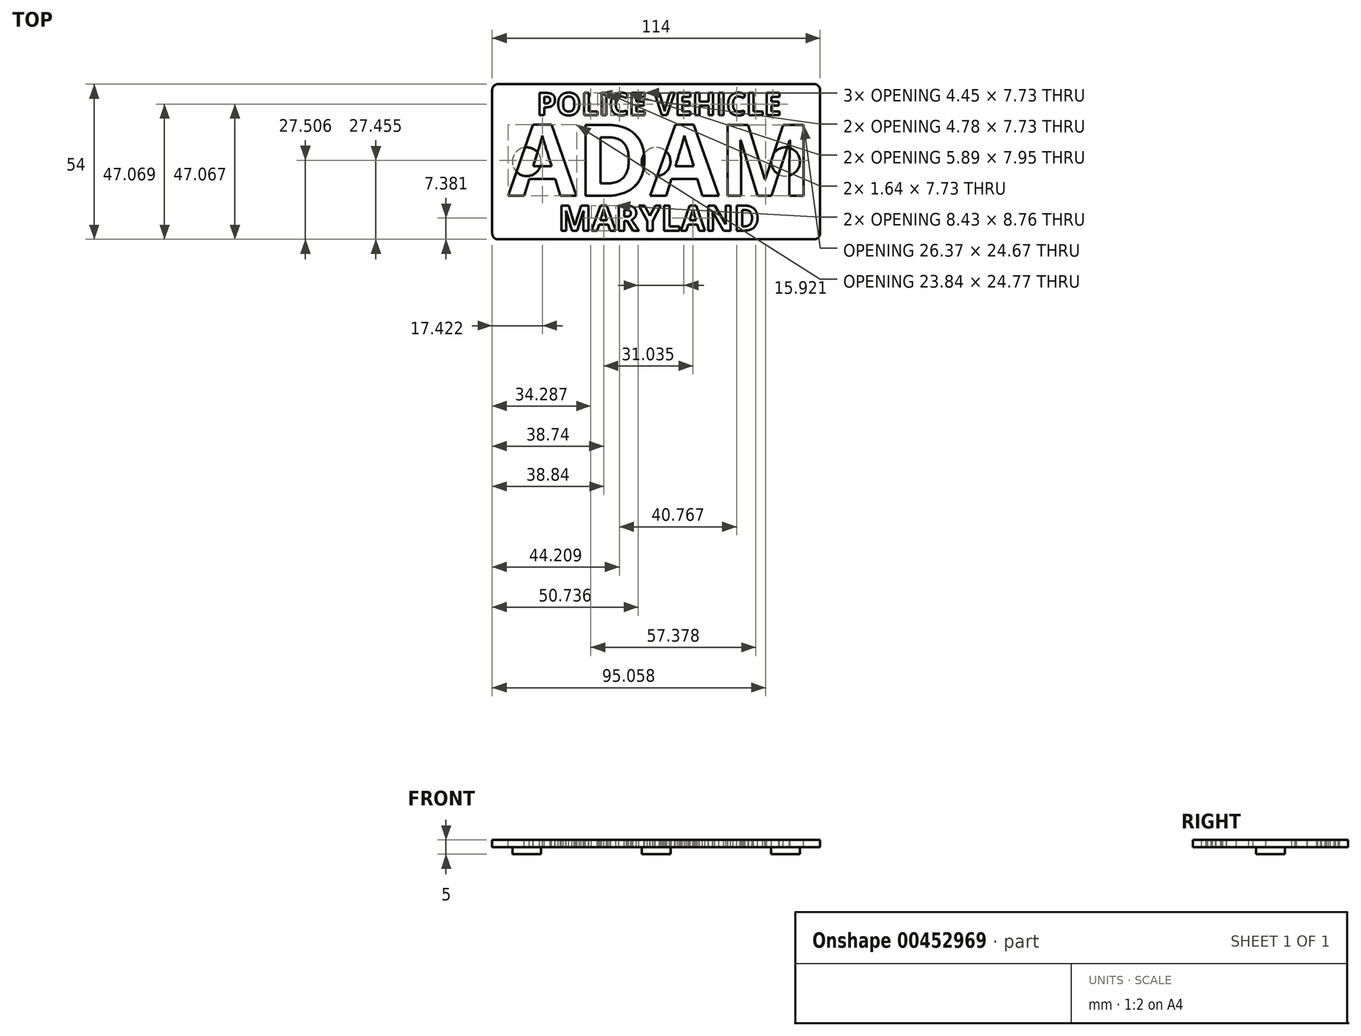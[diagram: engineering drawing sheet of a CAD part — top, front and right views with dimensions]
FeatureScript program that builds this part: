
annotation { "Feature Type Name" : "Feature", "Feature Type Description" : "" }
export const myFeature = defineFeature(function(context is Context, id is Id, definition is map)
    precondition{}
    {
        {
            var Q0;
            Q0=qCreatedBy(makeId("Top.planeOp"),FACE);
            var sketch = newSketch(context, id + "F0", { "sketchPlane" : qUnion([Q0])});
            skCircle(sketch, "E0", {"center": v(0, 0) * mm, "radius": 5 * mm});
            skCircle(sketch, "E1", {"center": v(-45, 0) * mm, "radius": 5 * mm});
            skCircle(sketch, "E2.MirrorC", {"center": v(45, 0) * mm, "radius": 5 * mm});
            skSolve(sketch);
        }
        {
            var Q0;
            Q0 = qSketchRegion(id + "F0", true);
            extrude(context, id + "F1", {"entities" : qUnion([Q0]), "depth" : 2.5 * mm, "offsetDistance" : 25 * mm});
        }
        {
            var Q0;
            Q0=qCreatedBy(makeId("Top.planeOp"),FACE);
            cPlane(context, id + "F2", {"entities" : qUnion([Q0]), "cplaneType" : CPlaneType.OFFSET, "offset" : 2.5 * mm, "width" : 150 * mm, "height" : 150 * mm});
        }
        {
            var Q0;
            Q0=qCreatedBy(id+"F2.planeOp",FACE);
            var sketch = newSketch(context, id + "F3", { "sketchPlane" : qUnion([Q0])});
            skLineSegment(sketch, "E3.bottom", {"start": v(57, -27) * mm, "end": v(-57, -27) * mm});
            skLineSegment(sketch, "E3.top", {"start": v(57, 27) * mm, "end": v(-57, 27) * mm});
            skLineSegment(sketch, "E3.left", {"start": v(57, -27) * mm, "end": v(57, 27) * mm});
            skLineSegment(sketch, "E3.right", {"start": v(-57, -27) * mm, "end": v(-57, 27) * mm});
            skPoint(sketch, "E3.middle", {"position": v(0, 0) * mm});
            skSolve(sketch);
        }
        {
            var Q0;
            Q0 = qSketchRegion(id + "F3", true);
            extrude(context, id + "F4", {"entities" : qUnion([Q0]), "operationType" : NewBodyOperationType.ADD, "depth" : 2.5 * mm, "offsetDistance" : 25 * mm});
        }
        {
            var Q0;
            Q0=makeQuery(id+"F4.opExtrude","CAP_FACE",FACE,{"disambiguationData":[OSD([sQuery(id+"F3.wireOp",EDGE,"E3.bottom"),sQuery(id+"F3.wireOp",EDGE,"E3.top"),sQuery(id+"F3.wireOp",EDGE,"E3.left"),sQuery(id+"F3.wireOp",EDGE,"E3.right")])],"isStart":false});
            var sketch = newSketch(context, id + "F5", { "sketchPlane" : qUnion([Q0])});
            skText(sketch, "E4", { "text": "ADAM", "fontName": "OpenSans-Bold.ttf"});
            skText(sketch, "E5", { "text": "MARYLAND", "fontName": "OpenSans-Bold.ttf"});
            skText(sketch, "E6", { "text": "POLICE VEHICLE\n", "fontName": "OpenSans-Bold.ttf"});
            skPoint(sketch, "E7.middle", {"position": v(0, 0) * mm});
            const initialGuessF5  = {"E4": [-0.0515, -0.01188, 1, 0, 0.02488], "E5": [-0.034, -0.024, 1, 0, 0.0088], "E6": [-0.0415, 0.0162, 1, 0, 0.0078]};
            skSetInitialGuess(sketch, initialGuessF5);
            skSolve(sketch);
        }
        {
            var Q0;
            Q0 = qSketchRegion(id + "F5", true);
            extrude(context, id + "F6", {"entities" : qUnion([Q0]), "operationType" : NewBodyOperationType.REMOVE, "oppositeDirection" : true, "depth" : 2.5 * mm, "offsetDistance" : 25 * mm});
        }
        {
            var Q0;
            Q0=makeQuery(id+"F4.opExtrude","SWEPT_EDGE",EDGE,{"disambiguationData":[OSD([sQuery(id+"F3.wireOp",EDGE,"E3.bottom"),sQuery(id+"F3.wireOp",EDGE,"E3.right")])]});
            var Q1;
            Q1=makeQuery(id+"F4.opExtrude","SWEPT_EDGE",EDGE,{"disambiguationData":[OSD([sQuery(id+"F3.wireOp",EDGE,"E3.bottom"),sQuery(id+"F3.wireOp",EDGE,"E3.left")])]});
            var Q2;
            Q2=makeQuery(id+"F4.opExtrude","SWEPT_EDGE",EDGE,{"disambiguationData":[OSD([sQuery(id+"F3.wireOp",EDGE,"E3.top"),sQuery(id+"F3.wireOp",EDGE,"E3.left")])]});
            var Q3;
            Q3=makeQuery(id+"F4.opExtrude","SWEPT_EDGE",EDGE,{"disambiguationData":[OSD([sQuery(id+"F3.wireOp",EDGE,"E3.top"),sQuery(id+"F3.wireOp",EDGE,"E3.right")])]});
            fillet(context, id + "F7", {"entities" : qUnion([Q0, Q1, Q2, Q3]), "radius" : 2 * mm, "tangentPropagation" : true, "allowEdgeOverflow" : false});
        }
    });
